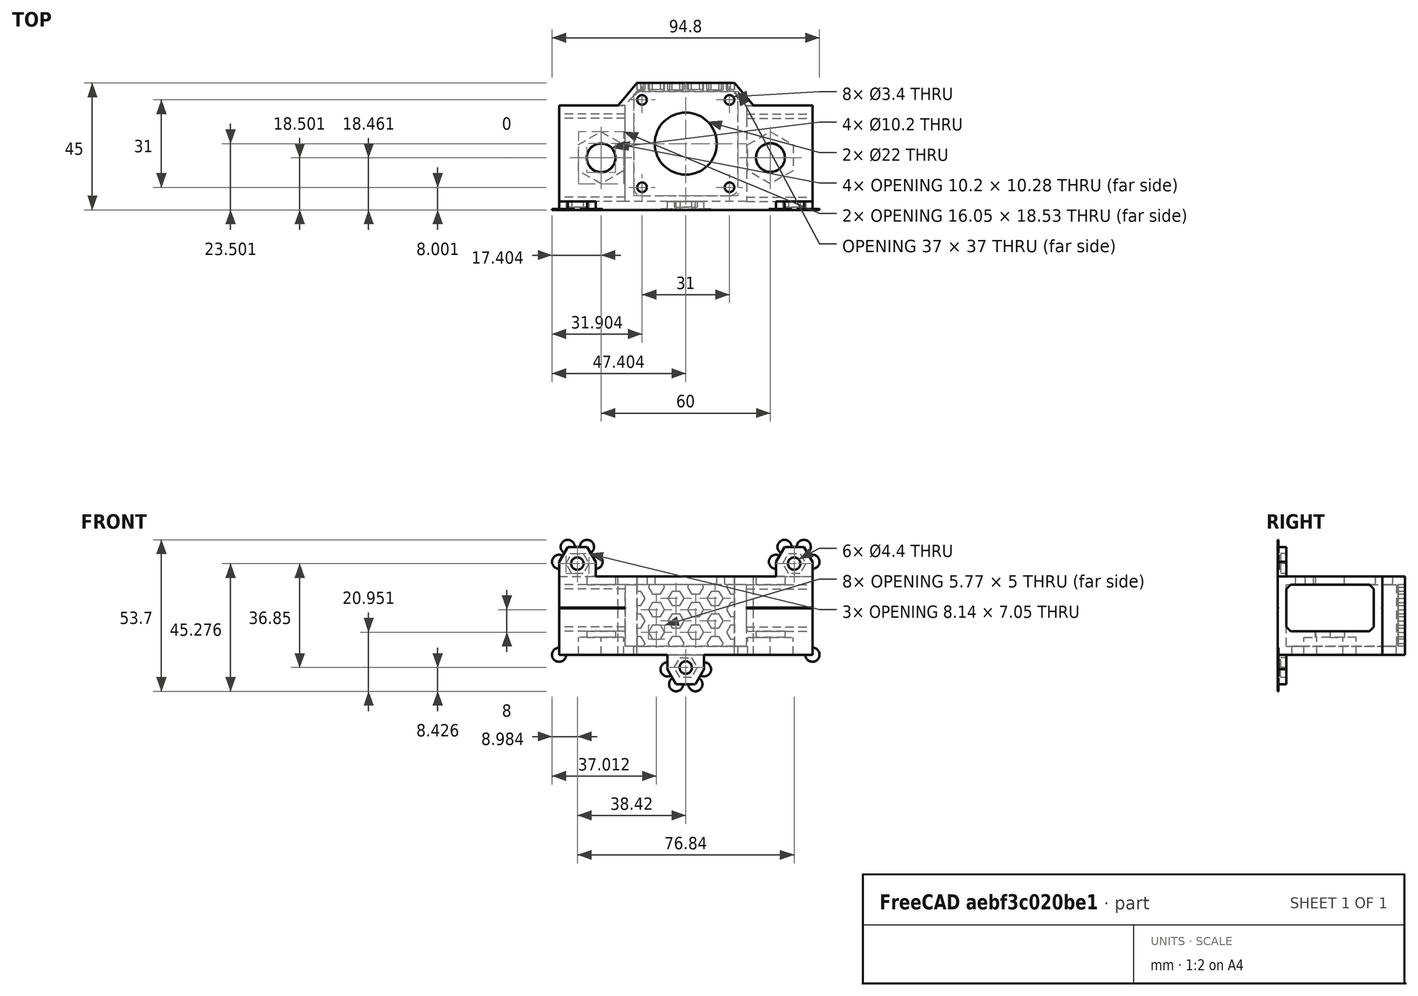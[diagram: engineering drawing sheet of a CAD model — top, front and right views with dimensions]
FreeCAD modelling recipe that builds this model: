
FCSTD DOCUMENT  (FreeCAD 0.15R4671 (Git))
Label: Halterung Schrittmotor v4 - Zusammenbau liegend
License: All rights reserved
LicenseURL: http://de.wikipedia.org/wiki/Alle_Rechte_vorbehalten
objects: Part::FeaturePython×6, Part::MultiFuse×1, Sketcher::SketchObject×1, PartDesign::Pad×1
note: 10 computed .brp shape members not serialized (recipe doc carries the construction recipe); baked Part::Feature solids carry a one-line shape summary decoded from their .brp

FEATURE [Part::FeaturePython] Halterung_Schrittmotor_v4___Motorhalter_01  # a2plus imported part (geometry in sourceFile) (typed FeaturePython)
  fixedPosition = true
  sourceFile = <userpath>/Documents/WORK/Halterung Schrittmotor v4 - Motorhalter.FCStd
  timeLastImport = 1.45002e+09
  updateColors = true
FEATURE [Part::FeaturePython] Halterung_Schritmotor_v4___Fuehrung_01  # a2plus imported part (geometry in sourceFile) (typed FeaturePython)
  Placement = pos=(30,-5,0) rot=(0,0,1;1.5708rad)
  fixedPosition = false
  sourceFile = <userpath>/Documents/WORK/Halterung Schritmotor v4 - Fuehrung.FCStd
  timeLastImport = 1449747062
  updateColors = true
FEATURE [Part::FeaturePython] Halterung_Schritmotor_v4___Fuehrung_  # a2plus imported part (geometry in sourceFile) (typed FeaturePython)
  Placement = pos=(-30,-5,0) rot=(0,0,-1;1.5708rad)
  fixedPosition = false
  sourceFile = <userpath>/Documents/WORK/Halterung Schritmotor v4 - Fuehrung.FCStd
  timeLastImport = 1449747062
  updateColors = true
FEATURE [Part::FeaturePython] Halterung_Schrittmotor_v4___Verschraubung_003  # a2plus imported part (geometry in sourceFile) (typed FeaturePython)
  Placement = pos=(38.42,-23.5,32.325) rot=(0,0.707107,0.707107;3.14159rad)
  fixedPosition = false
  sourceFile = <userpath>/Documents/WORK/Halterung Schrittmotor v4 - Verschraubung.FCStd
  timeLastImport = 1449057812
  updateColors = true
FEATURE [Part::FeaturePython] Halterung_Schrittmotor_v4___Verschraubung_004  # a2plus imported part (geometry in sourceFile) (typed FeaturePython)
  Placement = pos=(0,-23.5,-4.525) rot=(-1,0,0;1.5708rad)
  fixedPosition = false
  sourceFile = <userpath>/Documents/WORK/Halterung Schrittmotor v4 - Verschraubung.FCStd
  timeLastImport = 1449057812
  updateColors = true
FEATURE [Part::FeaturePython] Halterung_Schrittmotor_v4___Verschraubung_005  # a2plus imported part (geometry in sourceFile) (typed FeaturePython)
  Placement = pos=(-38.42,-23.5,32.325) rot=(0,0.707107,0.707107;3.14159rad)
  fixedPosition = false
  sourceFile = <userpath>/Documents/WORK/Halterung Schrittmotor v4 - Verschraubung.FCStd
  timeLastImport = 1449057812
  updateColors = true
FEATURE [Part::MultiFuse] Fusion  label="Halterung"
  Placement = pos=(12.3242,20.5006,-56.3191) rot=(0,0,1;0rad)
  Shapes = -> [Halterung_Schrittmotor_v4___Verschraubung_005,Halterung_Schrittmotor_v4___Verschraubung_004,Halterung_Schrittmotor_v4___Verschraubung_003,Halterung_Schritmotor_v4___Fuehrung_01,Halterung_Schrittmotor_v4___Motorhalter_01,Halterung_Schritmotor_v4___Fuehrung_]
FEATURE [Sketcher::SketchObject] Sketch
  ExternalGeometry = -> [Fusion]
  Placement = pos=(12.3242,-2.99941,-56.3191) rot=(1,0,0;1.5708rad)
  Support = -> Fusion [Face58]
  sketch-geometry (14):
    g0: Circle CenterX=-44.8903 CenterY=32.9681 CenterZ=0 NormalX=0 NormalY=0 NormalZ=1 Radius=2.5
    g1: Circle CenterX=-41.8408 CenterY=38.25 CenterZ=0 NormalX=0 NormalY=0 NormalZ=1 Radius=2.5
    g2: Circle CenterX=-34.9992 CenterY=38.25 CenterZ=0 NormalX=0 NormalY=0 NormalZ=1 Radius=2.5
    g3: Circle CenterX=-31.9497 CenterY=32.9681 CenterZ=0 NormalX=0 NormalY=0 NormalZ=1 Radius=2.5
    g4: Circle CenterX=41.8408 CenterY=38.25 CenterZ=0 NormalX=0 NormalY=0 NormalZ=1 Radius=2.5
    g5: Circle CenterX=44.8903 CenterY=32.9681 CenterZ=0 NormalX=0 NormalY=0 NormalZ=1 Radius=2.5
    g6: Circle CenterX=44.9 CenterY=0 CenterZ=0 NormalX=0 NormalY=0 NormalZ=1 Radius=2.5
    g7: Circle CenterX=6.47032 CenterY=-5.16808 CenterZ=0 NormalX=0 NormalY=0 NormalZ=1 Radius=2.5
    g8: Circle CenterX=3.4208 CenterY=-10.45 CenterZ=0 NormalX=0 NormalY=0 NormalZ=1 Radius=2.5
    g9: Circle CenterX=-3.4208 CenterY=-10.45 CenterZ=0 NormalX=0 NormalY=0 NormalZ=1 Radius=2.5
    g10: Circle CenterX=-6.47032 CenterY=-5.16808 CenterZ=0 NormalX=0 NormalY=0 NormalZ=1 Radius=2.5
    g11: Circle CenterX=-44.9 CenterY=0 CenterZ=0 NormalX=0 NormalY=0 NormalZ=1 Radius=2.5
    g12: Circle CenterX=31.9497 CenterY=32.9681 CenterZ=0 NormalX=0 NormalY=0 NormalZ=1 Radius=2.5
    g13: Circle CenterX=34.9992 CenterY=38.25 CenterZ=0 NormalX=0 NormalY=0 NormalZ=1 Radius=2.5
  constraints (16):
    c: Coincident(g0,g-8)
    c: Coincident(g1,g-8)
    c: Coincident(g2,g-9)
    c: Coincident(g3,g-9)
    c: Coincident(g4,g-7)
    c: Coincident(g5,g-7)
    c: Coincident(g6,g-4)
    c: Coincident(g7,g-5)
    c: Coincident(g8,g-5)
    c: Coincident(g9,g-6)
    c: Coincident(g10,g-6)
    c: Coincident(g11,g-3)
    c: Coincident(g12,g-10)
    c: Coincident(g13,g-10)
    c: Radius(g0) = 2.5
    c: Equal(g0, g1-g13) x13
FEATURE [PartDesign::Pad] Pad  label="Halterung druckbar"
  Length = 0.3
  Length2 = 100
  Placement = pos=(12.3242,20.5006,-56.3191) rot=(0,0,1;0rad)
  Reversed = true
  Sketch = -> Sketch
  Type = 0
